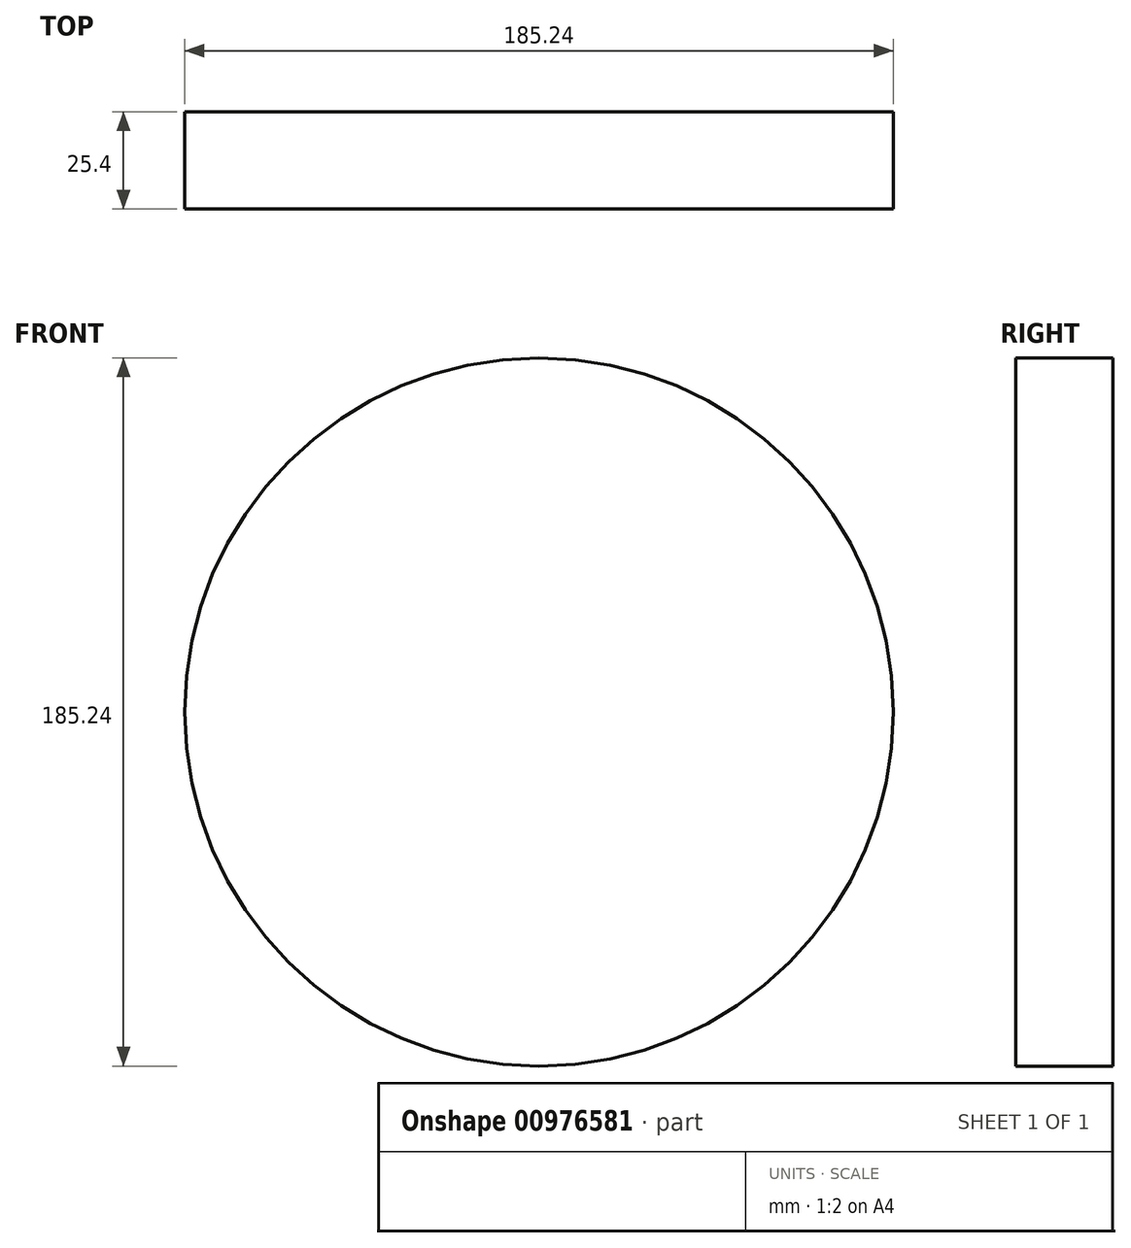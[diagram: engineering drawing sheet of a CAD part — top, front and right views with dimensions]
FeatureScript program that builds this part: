
annotation { "Feature Type Name" : "Feature", "Feature Type Description" : "" }
export const myFeature = defineFeature(function(context is Context, id is Id, definition is map)
    precondition{}
    {
        {
            var Q0;
            Q0=qCreatedBy(makeId("Front.planeOp"),FACE);
            var sketch = newSketch(context, id + "F0", { "sketchPlane" : qUnion([Q0])});
            skCircle(sketch, "E0", {"center": v(-12.43, 23.6) * mm, "radius": 92.62 * mm});
            skSolve(sketch);
        }
        {
            var Q0;
            Q0=makeQuery(id+"F0.imprint","IMPRINT",FACE,{"disambiguationData":[TD([[makeQuery(id+"F0.imprint","IMPRINT",EDGE,{"derivedFrom":sQuery(id+"F0.wireOp",EDGE,"E0")}),1.0]])]});
            extrude(context, id + "F1", {"entities" : qUnion([Q0]), "depth" : 25.4 * mm, "offsetDistance" : 25.4 * mm});
        }
    });
